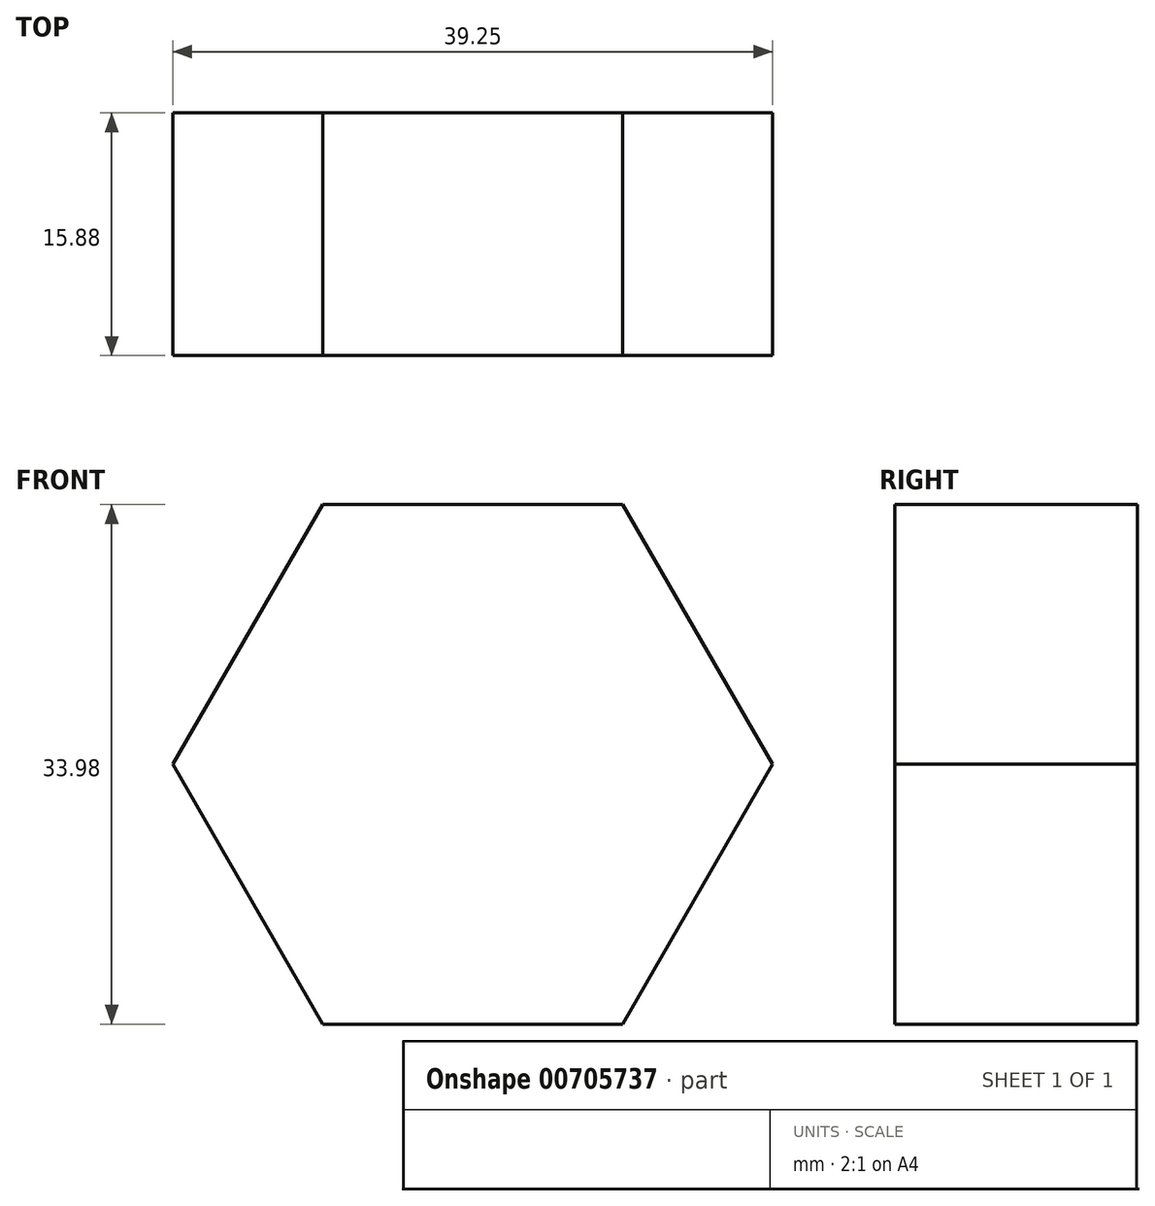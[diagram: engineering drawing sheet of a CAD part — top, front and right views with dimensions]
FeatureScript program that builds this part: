
annotation { "Feature Type Name" : "Feature", "Feature Type Description" : "" }
export const myFeature = defineFeature(function(context is Context, id is Id, definition is map)
    precondition{}
    {
        {
            var Q0;
            Q0=qCreatedBy(makeId("Front.planeOp"),FACE);
            var sketch = newSketch(context, id + "F0", { "sketchPlane" : qUnion([Q0])});
            skCircle(sketch, "E0.cCircle", {"center": v(-0.57, 0) * mm, "radius": 17 * mm, "construction": true});
            skLineSegment(sketch, "E0.0", {"start": v(-20.19, 0) * mm, "end": v(-10.38, 17) * mm});
            skLineSegment(sketch, "E0.1", {"start": v(-10.38, 17) * mm, "end": v(9.25, 17) * mm});
            skLineSegment(sketch, "E0.2", {"start": v(9.25, 17) * mm, "end": v(19.06, 0) * mm});
            skLineSegment(sketch, "E0.3", {"start": v(19.06, 0) * mm, "end": v(9.25, -17) * mm});
            skLineSegment(sketch, "E0.4", {"start": v(9.25, -17) * mm, "end": v(-10.38, -17) * mm});
            skLineSegment(sketch, "E0.5", {"start": v(-10.38, -17) * mm, "end": v(-20.19, 0) * mm});
            skPoint(sketch, "E0.0.midPoint", {"position": v(-15.28, 8.5) * mm});
            skSolve(sketch);
        }
        {
            var Q0;
            Q0 = qSketchRegion(id + "F0", true);
            extrude(context, id + "F1", {"entities" : qUnion([Q0]), "depth" : 15.88 * mm, "offsetDistance" : 25.4 * mm});
        }
    });
